# Revit family: ERA_LF_PR_SPO-114
name_source: partatom
category: Осветительные приборы
units: mm (PartAtom-declared; Revit-internal decimal feet)

## family parameters
Всегда вертикально = Да
Заголовок OmniClass = Lighting
Источник света = Да
На основе рабочей плоскости = Нет
Номер OmniClass = 23.80.70.00
Общий = Нет
При загрузке вырезать с полостями = Нет
Размер круглого соединителя = Использовать диаметр
Тип детали = Нормальный
Точка расчета площади = Да

## types (2) — shared parameters
ADSK_Единица измерения = шт.
ADSK_Завод-изготовитель = ЭРА
ADSK_Классификация нагрузок = Освещение
ADSK_Количество фаз = 1
ADSK_Коэффициент мощности = 0.95
ADSK_Масса = 1.7
ADSK_Наименование = Светильник, LED, прямоугольный, подвесной, IP40, 1200х130х50 мм (ДхШхВ), 36 Вт, 4000 К, 2800 лм, класс защиты I, в комплекте (импульсный драйвер без гальваничесокй развязки)
ADSK_Наименование краткое = Светильник
ADSK_Напряжение = 230 В
ADSK_Номинальная мощность = 36 Вт
ADSK_Полная мощность = 38 В·А
ADSK_Примечание = Импульсный драйвер
ADSK_Размер_Высота = 50 мм
ADSK_Размер_Длина = 1200 мм
ADSK_Размер_Ширина = 130 мм
URL = https://www.eraworld.ru
_Корпус_Высота = 50 мм
_Корпус_Диаметр = 1 мм
_Корпус_Длина = 1200 мм
_Корпус_Ширина = 130 мм
_Подвес_Диаметр = 1 мм
_Подвес_Расстояние = 1150 мм
_Подвес_Чаша_Высота = 20 мм
_Подвес_Чаша_Диаметр = 10 мм
_УГО_Диаметр = 12 мм
_УГО_Длина = 12 мм
_УГО_Ширина = 1.3 мм
Видимая форма излучения при визуализации = Нет
Высота чаши подвеса = 20 мм
Геометрия изделия = Прямоугольный
Диаметр подвеса = 1 мм
Диаметр чаши подвеса = 10 мм
Излучение по длине прямоугольника = 1200 мм
Излучение по ширине прямоугольника = 130 мм
Источник света = LED
Класс защиты = I
Комплект = Импульсный драйвер без гальваничесокй развязки
Разработчик модели = https://www.teslabim.ru
Светофильтр = 16777215
Смещение цветовой температуры при затухании лампы = <Нет>
Степень защиты IP = IP40
Тип установки = Подвесной
УГО_Масштаб = 100
Угол наклона = 90,00°
Файл фотометрической сетки = SPO-114-W-40K-036.ies
zero-valued in all types: ADSK_Размер_Диаметр

## per-type parameters (varying)
| type | ADSK_Марка | ADSK_Обозначение | Цвет |
| SPO-114-W-40K-036, LED, IP40, 1200х130х50 мм (ДхШхВ), 36 Вт, 4000 К, 2800 лм, класс защиты I, в комплекте (импульсный драйвер без гальваничесокй развязки) | SPO-114-W-40K-036 | SPO-114-W-40K-036 | Белый |
| SPO-114-B-40K-036, LED, IP40, 1200х130х50 мм (ДхШхВ), 36 Вт, 4000 К, 2800 лм, класс защиты I, в комплекте (импульсный драйвер без гальваничесокй развязки) | SPO-114-B-40K-036 | SPO-114-B-40K-036 | Чёрный |
